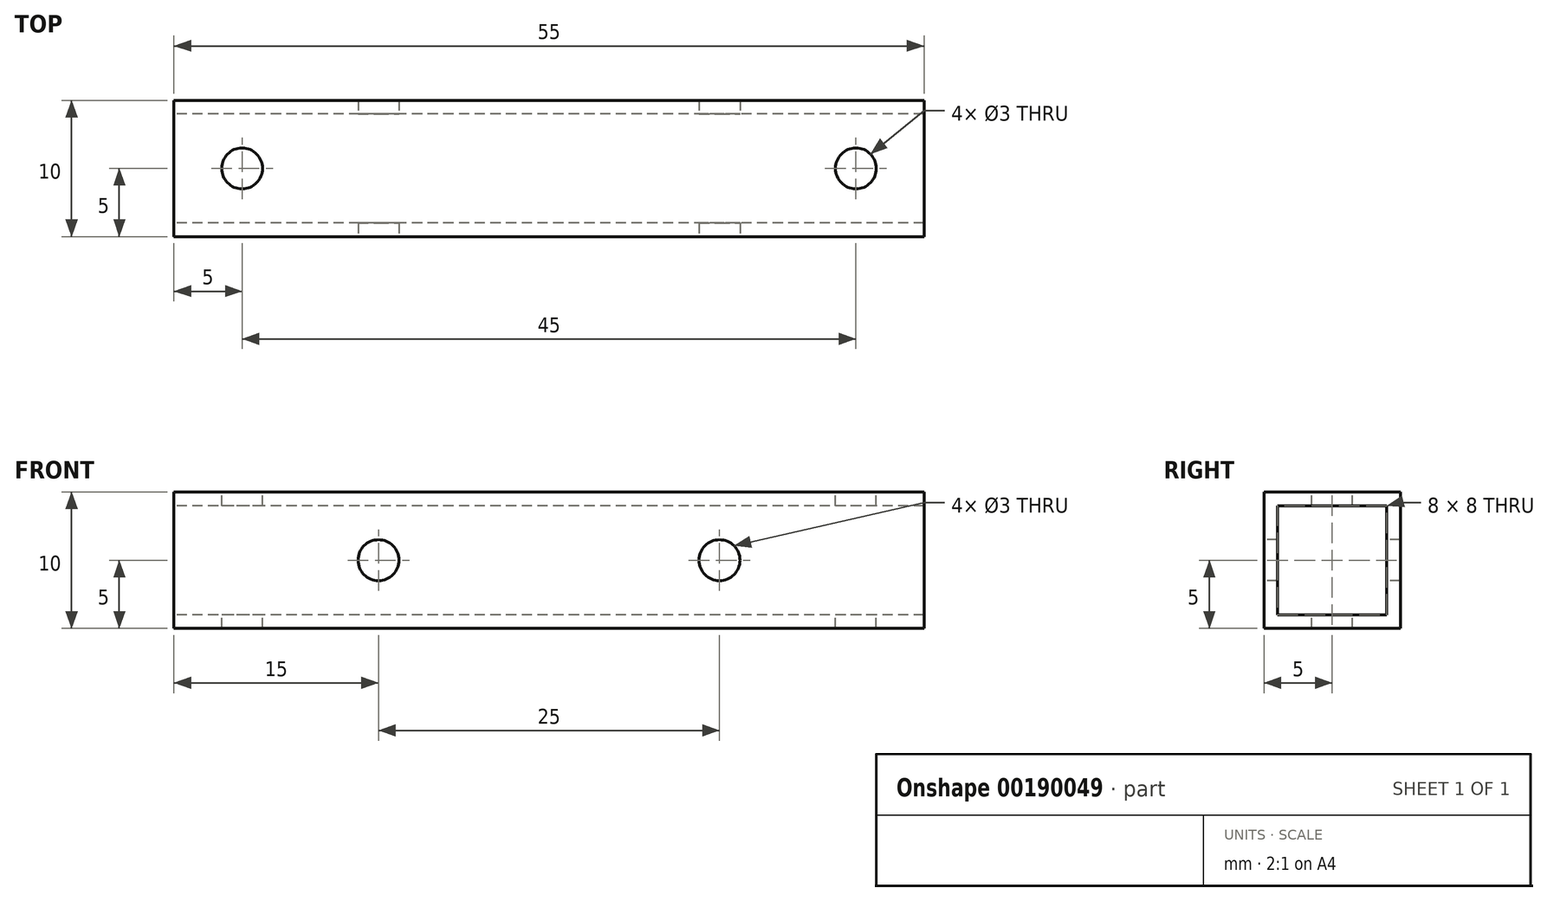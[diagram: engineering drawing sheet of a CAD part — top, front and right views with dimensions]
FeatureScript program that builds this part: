
annotation { "Feature Type Name" : "Feature", "Feature Type Description" : "" }
export const myFeature = defineFeature(function(context is Context, id is Id, definition is map)
    precondition{}
    {
        {
            var Q0;
            Q0=qCreatedBy(makeId("Right.planeOp"),FACE);
            var sketch = newSketch(context, id + "F0", { "sketchPlane" : qUnion([Q0])});
            skLineSegment(sketch, "E0.bottom", {"start": v(-5, -5) * mm, "end": v(5, -5) * mm});
            skLineSegment(sketch, "E0.top", {"start": v(-5, 5) * mm, "end": v(5, 5) * mm});
            skLineSegment(sketch, "E0.left", {"start": v(-5, -5) * mm, "end": v(-5, 5) * mm});
            skLineSegment(sketch, "E0.right", {"start": v(5, -5) * mm, "end": v(5, 5) * mm});
            skPoint(sketch, "E0.middle", {"position": v(0, 0) * mm});
            skLineSegment(sketch, "E1.bottom", {"start": v(-4, -4) * mm, "end": v(4, -4) * mm});
            skLineSegment(sketch, "E1.top", {"start": v(-4, 4) * mm, "end": v(4, 4) * mm});
            skLineSegment(sketch, "E1.left", {"start": v(-4, -4) * mm, "end": v(-4, 4) * mm});
            skLineSegment(sketch, "E1.right", {"start": v(4, -4) * mm, "end": v(4, 4) * mm});
            skSolve(sketch);
        }
        {
            var Q0;
            Q0 = qSketchRegion(id + "F0", true);
            extrude(context, id + "F1", {"entities" : qUnion([Q0]), "depth" : 55 * mm});
        }
        {
            var Q0;
            Q0=makeQuery(id+"F1.opExtrude","SWEPT_FACE",FACE,{"disambiguationData":[OSD([sQuery(id+"F0.wireOp",EDGE,"E0.top")])]});
            var sketch = newSketch(context, id + "F2", { "sketchPlane" : qUnion([Q0])});
            skLineSegment(sketch, "E2", {"start": v(0, 0) * mm, "end": v(55, 0) * mm, "construction": true});
            skLineSegment(sketch, "E3", {"start": v(27.5, 5) * mm, "end": v(27.5, -5) * mm, "construction": true});
            skCircle(sketch, "E4", {"center": v(5, 0) * mm, "radius": 1.5 * mm});
            skCircle(sketch, "E5.MirrorC", {"center": v(50, 0) * mm, "radius": 1.5 * mm});
            skSolve(sketch);
        }
        {
            var Q0;
            Q0 = qSketchRegion(id + "F2", true);
            extrude(context, id + "F3", {"entities" : qUnion([Q0]), "operationType" : NewBodyOperationType.REMOVE, "oppositeDirection" : true, "depth" : 25 * mm});
        }
        {
            var Q0;
            Q0=makeQuery(id+"F1.opExtrude","SWEPT_FACE",FACE,{"disambiguationData":[OSD([sQuery(id+"F0.wireOp",EDGE,"E0.left")])]});
            var sketch = newSketch(context, id + "F4", { "sketchPlane" : qUnion([Q0])});
            skLineSegment(sketch, "E6", {"start": v(0, 0) * mm, "end": v(55, 0) * mm, "construction": true});
            skLineSegment(sketch, "E7", {"start": v(27.5, 5) * mm, "end": v(27.5, -5) * mm, "construction": true});
            skCircle(sketch, "E8", {"center": v(15, 0) * mm, "radius": 1.5 * mm});
            skCircle(sketch, "E9.MirrorC", {"center": v(40, 0) * mm, "radius": 1.5 * mm});
            skSolve(sketch);
        }
        {
            var Q0;
            Q0 = qSketchRegion(id + "F4", true);
            extrude(context, id + "F5", {"entities" : qUnion([Q0]), "operationType" : NewBodyOperationType.REMOVE, "oppositeDirection" : true, "depth" : 25 * mm});
        }
    });
